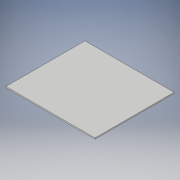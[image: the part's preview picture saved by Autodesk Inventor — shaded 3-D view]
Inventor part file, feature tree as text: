
AUTODESK INVENTOR PART (.ipt)
format: ipt  version: 2018 (Build 220112000, 112)  size: 90,112 bytes
history: native  units: in
note: dims shown in document units (in); Inventor stores cm internally (conversion verified against a paired STEP export)
features: extrude x1, sketch x1
ambient origin geometry x8: Origin, YZ Plane, XZ Plane, XY Plane, X Axis, Y Axis, Z Axis, Center Point
bodies: Solid1 (feature_tree)
feature tree (2):
  extrude  "Extrusion1"  Depth=2.1654in
  sketch  "Sketch1"  dims[d0=2.4409in d1=2.1654in d2=0.031in d3=0.0in]
